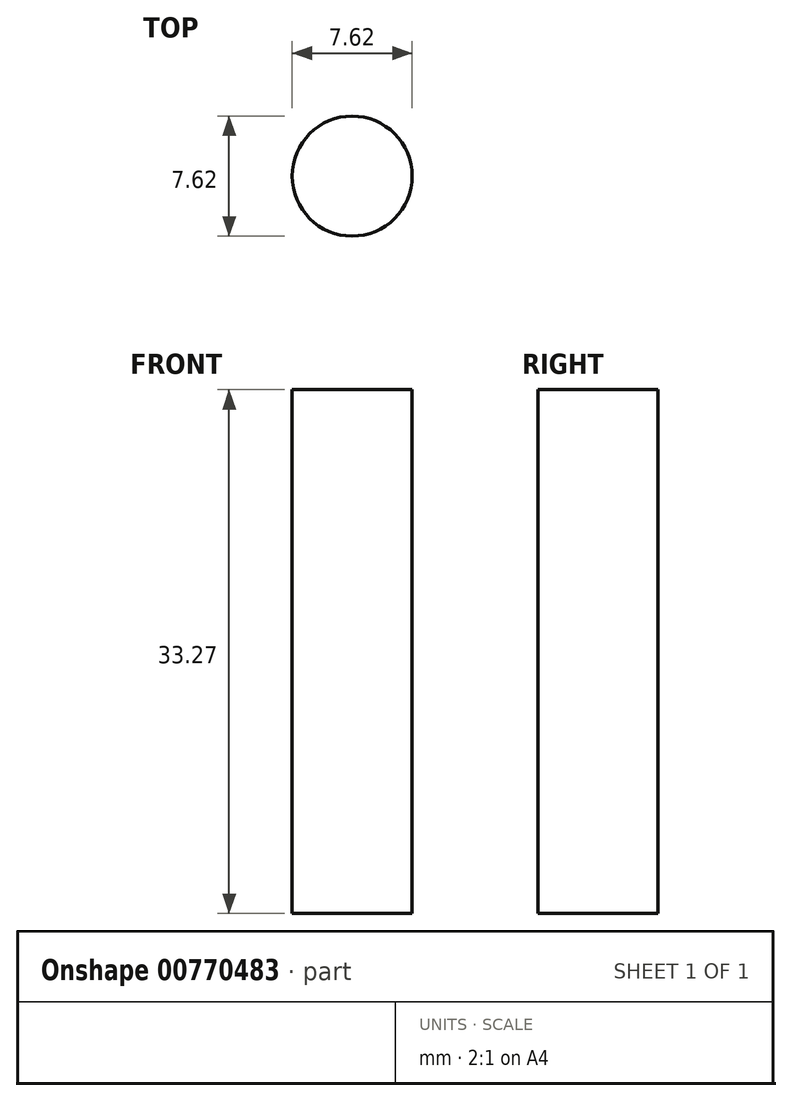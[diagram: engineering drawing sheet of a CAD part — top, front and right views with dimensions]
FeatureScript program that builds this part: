
annotation { "Feature Type Name" : "Feature", "Feature Type Description" : "" }
export const myFeature = defineFeature(function(context is Context, id is Id, definition is map)
    precondition{}
    {
        {
            var Q0;
            Q0=qCreatedBy(makeId("Top.planeOp"),FACE);
            var sketch = newSketch(context, id + "F0", { "sketchPlane" : qUnion([Q0])});
            skCircle(sketch, "E0", {"center": v(0, 0) * mm, "radius": 3.81 * mm});
            skSolve(sketch);
        }
        {
            var Q0;
            Q0=makeQuery(id+"F0.imprint","IMPRINT",FACE,{"disambiguationData":[TD([[makeQuery(id+"F0.imprint","IMPRINT",EDGE,{"derivedFrom":sQuery(id+"F0.wireOp",EDGE,"E0")}),1.0]])]});
            extrude(context, id + "F1", {"entities" : qUnion([Q0]), "depth" : 33.27 * mm, "offsetDistance" : 25.4 * mm});
        }
    });
